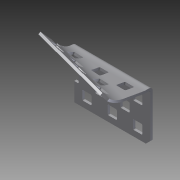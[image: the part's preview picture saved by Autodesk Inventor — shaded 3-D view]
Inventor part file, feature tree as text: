
AUTODESK INVENTOR PART (.ipt)
format: ipt  version: 2014 SP1 (Build 180222100, 222)  size: 539,136 bytes
history: native  units: in
note: dims shown in document units (in); Inventor stores cm internally (conversion verified against a paired STEP export)
features: other x3, sketch x3
ambient origin geometry x8: Origin, YZ Plane, XZ Plane, XY Plane, X Axis, Y Axis, Z Axis, Center Point
bodies: Solid1 (feature_tree)
feature tree (6):
  other  "2 x 3 bent for 169A rev5 hardstop.ipt"
  other  "NONE::2 x 3 bent for 169A rev5 hardstop.ipt"
  other  "TaggingFeature1"
  sketch  "Sketch1"  dims[d0=0.3937in]
  sketch  "Sketch3"  dims[d1=0.0in d2=6.0in d3=0.5in d4=0.2749in d5=0.5in d6=0.0687in]
  sketch  "Sketch4"
